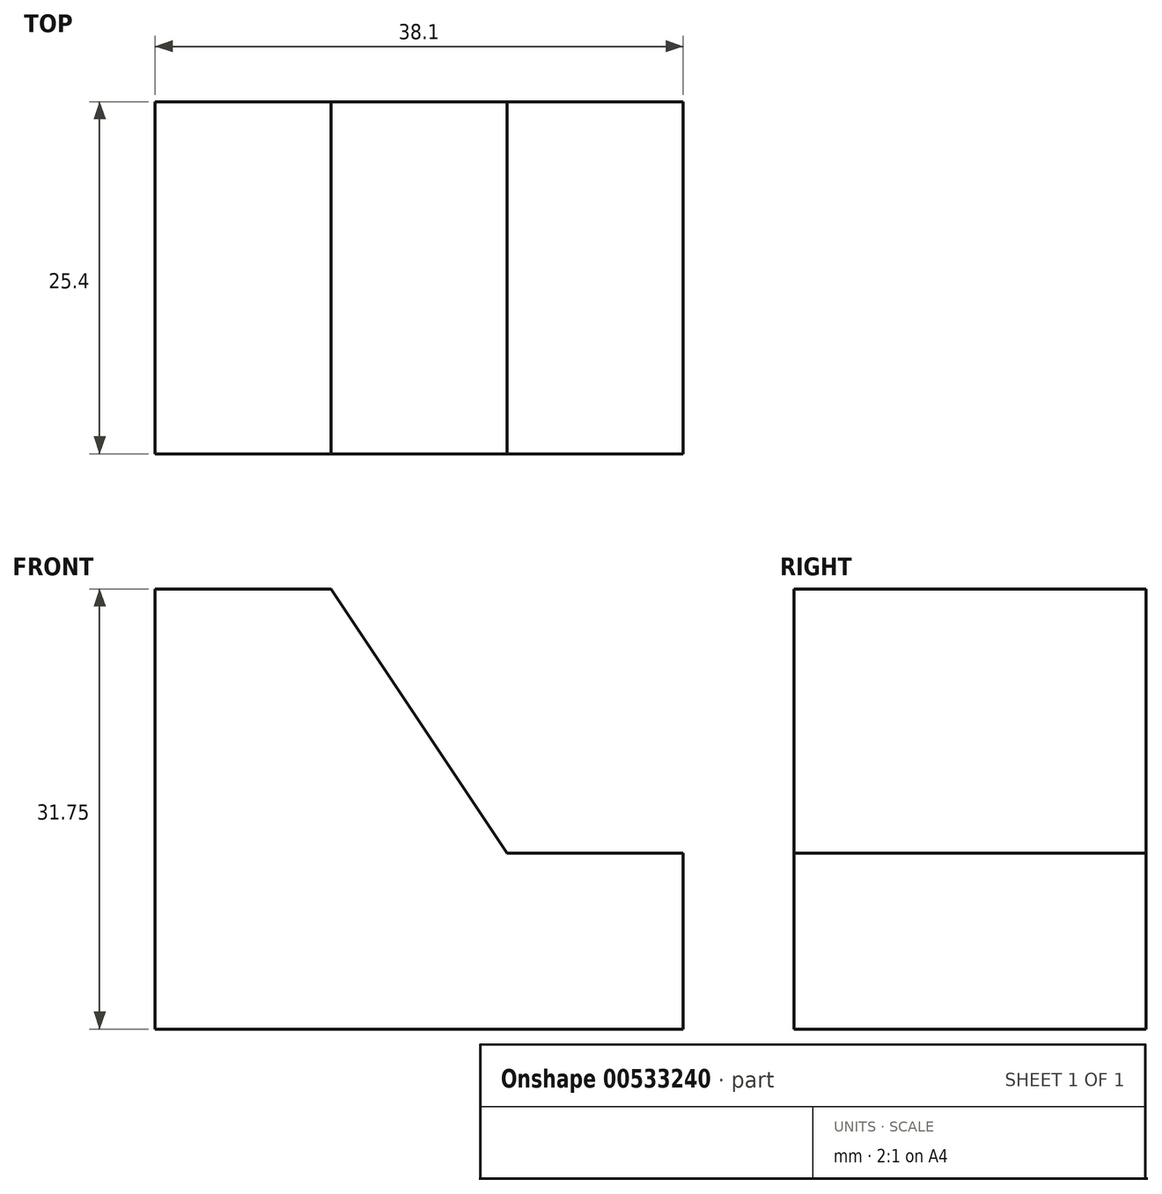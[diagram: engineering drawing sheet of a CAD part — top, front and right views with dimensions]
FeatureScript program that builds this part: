
annotation { "Feature Type Name" : "Feature", "Feature Type Description" : "" }
export const myFeature = defineFeature(function(context is Context, id is Id, definition is map)
    precondition{}
    {
        {
            var Q0;
            Q0=qCreatedBy(makeId("Front.planeOp"),FACE);
            var sketch = newSketch(context, id + "F0", { "sketchPlane" : qUnion([Q0])});
            skLineSegment(sketch, "E0", {"start": v(-81.87, 64.16) * mm, "end": v(-81.87, 32.4) * mm});
            skLineSegment(sketch, "E1", {"start": v(-81.87, 32.4) * mm, "end": v(-43.77, 32.4) * mm});
            skLineSegment(sketch, "E2", {"start": v(-43.77, 32.4) * mm, "end": v(-43.77, 45.1) * mm});
            skLineSegment(sketch, "E3", {"start": v(-43.77, 45.1) * mm, "end": v(-56.47, 45.1) * mm});
            skLineSegment(sketch, "E4", {"start": v(-81.87, 64.16) * mm, "end": v(-69.17, 64.16) * mm});
            skLineSegment(sketch, "E5", {"start": v(-69.17, 64.16) * mm, "end": v(-56.47, 45.1) * mm});
            skSolve(sketch);
        }
        {
            var Q0;
            Q0=makeQuery(id+"F0.imprint","IMPRINT",FACE,{"disambiguationData":[TD([[makeQuery(id+"F0.imprint","IMPRINT",EDGE,{"derivedFrom":sQuery(id+"F0.wireOp",EDGE,"E0")}),1.0]])]});
            extrude(context, id + "F1", {"entities" : qUnion([Q0]), "depth" : 25.4 * mm, "offsetDistance" : 25.4 * mm});
        }
    });
